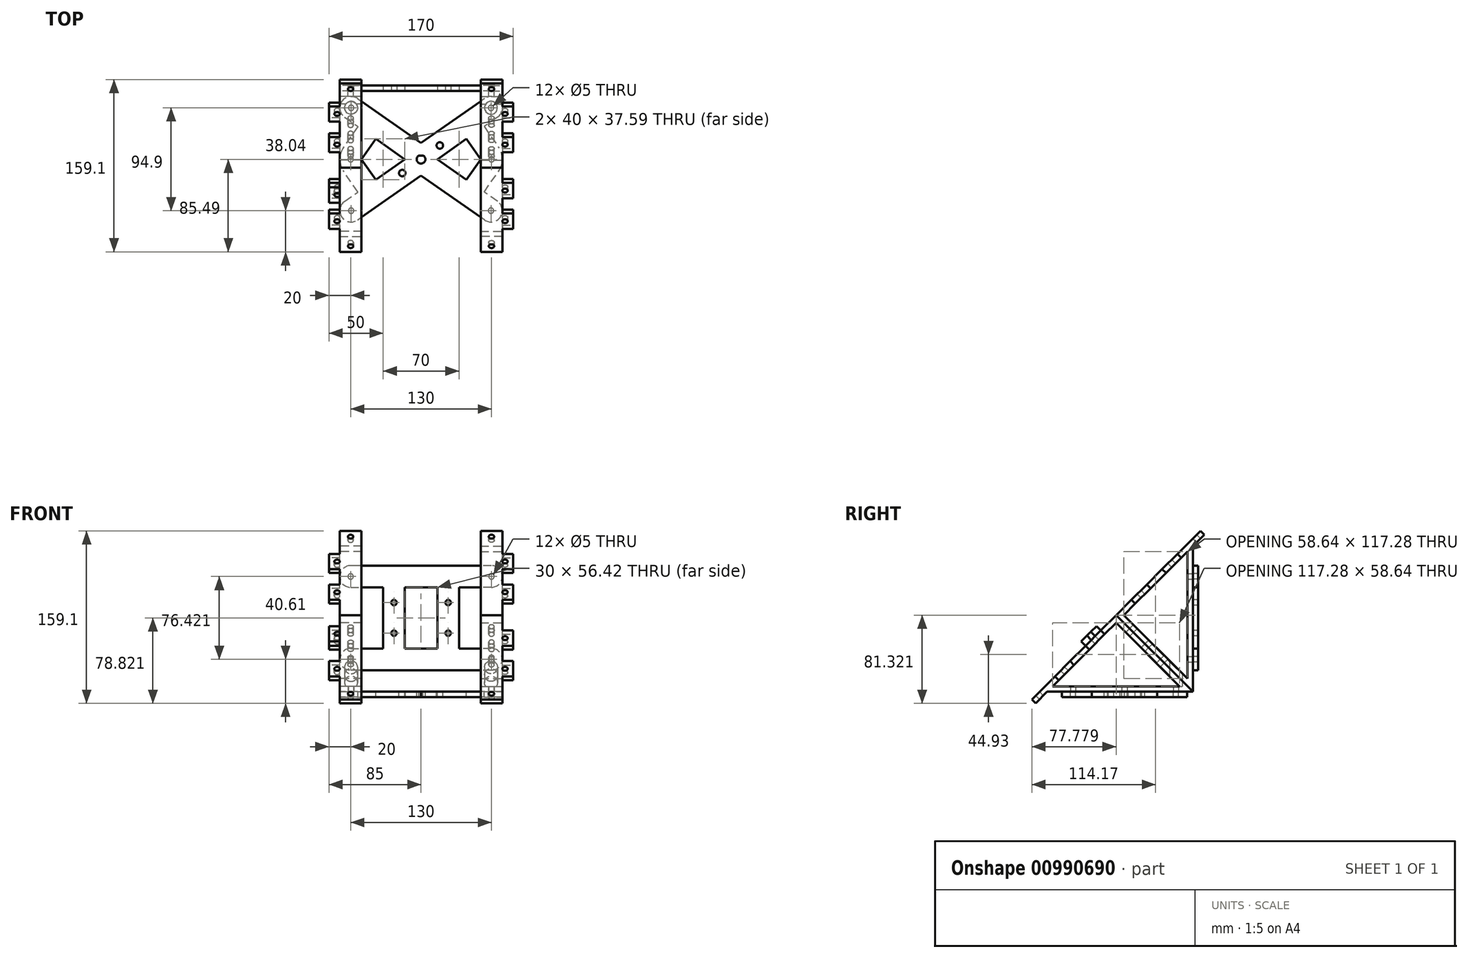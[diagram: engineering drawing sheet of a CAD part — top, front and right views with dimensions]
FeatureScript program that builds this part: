
annotation { "Feature Type Name" : "Feature", "Feature Type Description" : "" }
export const myFeature = defineFeature(function(context is Context, id is Id, definition is map)
    precondition{}
    {
        {
            var Q0;
            Q0=qCreatedBy(makeId("Right.planeOp"),FACE);
            var sketch = newSketch(context, id + "F0", { "sketchPlane" : qUnion([Q0])});
            skLineSegment(sketch, "E0", {"start": v(0, 0) * mm, "end": v(0, 141.42) * mm, "construction": true});
            skLineSegment(sketch, "E1", {"start": v(-141.42, 0) * mm, "end": v(0, 0) * mm});
            skLineSegment(sketch, "E2", {"start": v(0, 0) * mm, "end": v(-70.71, 70.71) * mm});
            skLineSegment(sketch, "E3", {"start": v(-141.42, 0) * mm, "end": v(-70.71, 70.71) * mm});
            skLineSegment(sketch, "E4", {"start": v(-70.71, 70.71) * mm, "end": v(0, 141.42) * mm, "construction": true});
            skLineSegment(sketch, "E5.0", {"start": v(-129.35, 5) * mm, "end": v(-70.71, 63.64) * mm});
            skLineSegment(sketch, "E5.1", {"start": v(-129.35, 5) * mm, "end": v(-12.07, 5) * mm});
            skLineSegment(sketch, "E5.2", {"start": v(-12.07, 5) * mm, "end": v(-70.71, 63.64) * mm});
            skLineSegment(sketch, "E6.0", {"start": v(-63.64, 70.71) * mm, "end": v(-5, 129.35) * mm, "construction": true});
            skLineSegment(sketch, "E6.1", {"start": v(-5, 12.07) * mm, "end": v(-63.64, 70.71) * mm, "construction": true});
            skLineSegment(sketch, "E6.2", {"start": v(-5, 12.07) * mm, "end": v(-5, 129.35) * mm, "construction": true});
            skSolve(sketch);
        }
        {
            var Q0;
            Q0=qCreatedBy(makeId("Right.planeOp"),FACE);
            var sketch = newSketch(context, id + "F1", { "sketchPlane" : qUnion([Q0])});
            skLineSegment(sketch, "E7", {"start": v(0, 0) * mm, "end": v(0, 141.42) * mm});
            skLineSegment(sketch, "E8", {"start": v(-141.42, 0) * mm, "end": v(0, 0) * mm, "construction": true});
            skLineSegment(sketch, "E9", {"start": v(0, 0) * mm, "end": v(-70.71, 70.71) * mm});
            skLineSegment(sketch, "E10", {"start": v(-141.42, 0) * mm, "end": v(-70.71, 70.71) * mm, "construction": true});
            skLineSegment(sketch, "E11", {"start": v(-70.71, 70.71) * mm, "end": v(0, 141.42) * mm});
            skLineSegment(sketch, "E12.0", {"start": v(-129.35, 5) * mm, "end": v(-70.71, 63.64) * mm, "construction": true});
            skLineSegment(sketch, "E12.1", {"start": v(-129.35, 5) * mm, "end": v(-12.07, 5) * mm, "construction": true});
            skLineSegment(sketch, "E12.2", {"start": v(-12.07, 5) * mm, "end": v(-70.71, 63.64) * mm, "construction": true});
            skLineSegment(sketch, "E13.0", {"start": v(-63.64, 70.71) * mm, "end": v(-5, 129.35) * mm});
            skLineSegment(sketch, "E13.1", {"start": v(-5, 12.07) * mm, "end": v(-63.64, 70.71) * mm});
            skLineSegment(sketch, "E13.2", {"start": v(-5, 12.07) * mm, "end": v(-5, 129.35) * mm});
            skSolve(sketch);
        }
        {
            var Q0;
            Q0 = qSketchRegion(id + "F0", true);
            extrude(context, id + "F2", {"entities" : qUnion([Q0]), "depth" : 20 * mm, "offsetDistance" : 25 * mm});
        }
        {
            var Q0;
            Q0 = qSketchRegion(id + "F1", true);
            extrude(context, id + "F3", {"entities" : qUnion([Q0]), "depth" : 20 * mm, "offsetDistance" : 25 * mm});
        }
        {
            var Q0;
            Q0=qCreatedBy(makeId("Top.planeOp"),FACE);
            var sketch = newSketch(context, id + "F4", { "sketchPlane" : qUnion([Q0])});
            skLineSegment(sketch, "E14", {"start": v(73.06, -59.5) * mm, "end": v(76.94, -59.5) * mm});
            skArc(sketch, "E15", {"start": v(73.06, -59.5) * mm, "mid": v(75, -67) * mm, "end": v(76.94, -59.5) * mm});
            skLineSegment(sketch, "E16.bottom", {"start": v(105, -93) * mm, "end": v(45, -93) * mm, "construction": true});
            skLineSegment(sketch, "E16.top", {"start": v(105, -33) * mm, "end": v(45, -33) * mm, "construction": true});
            skLineSegment(sketch, "E16.left", {"start": v(105, -93) * mm, "end": v(105, -33) * mm, "construction": true});
            skLineSegment(sketch, "E16.right", {"start": v(45, -93) * mm, "end": v(45, -33) * mm, "construction": true});
            skLineSegment(sketch, "E17", {"start": v(75, -63) * mm, "end": v(45, -63) * mm, "construction": true});
            skPoint(sketch, "E18.endSnap0", {"position": v(75, -93) * mm});
            skLineSegment(sketch, "E19", {"start": v(60, -63) * mm, "end": v(4.45, -101.9) * mm, "construction": true});
            skLineSegment(sketch, "E20", {"start": v(4.45, -101.9) * mm, "end": v(16.44, -119) * mm, "construction": true});
            skLineSegment(sketch, "E21", {"start": v(16.44, -119) * mm, "end": v(75, -78) * mm});
            skArc(sketch, "E22", {"start": v(4.45, -101.9) * mm, "mid": v(1.89, -116.44) * mm, "end": v(16.44, -119) * mm});
            skLineSegment(sketch, "E23", {"start": v(75, -63) * mm, "end": v(75, -93) * mm, "construction": true});
            skLineSegment(sketch, "E24.MirrorCS", {"start": v(75, -63) * mm, "end": v(105, -63) * mm, "construction": true});
            skLineSegment(sketch, "E25", {"start": v(60, -63) * mm, "end": v(33.16, -81.8) * mm});
            skLineSegment(sketch, "E26", {"start": v(33.16, -81.8) * mm, "end": v(20, -63) * mm});
            skLineSegment(sketch, "E27", {"start": v(4.45, -101.9) * mm, "end": v(16.78, -93.27) * mm});
            skLineSegment(sketch, "E28", {"start": v(16.78, -93.27) * mm, "end": v(3.62, -74.47) * mm});
            skArc(sketch, "E29", {"start": v(0, -63) * mm, "mid": v(0.93, -69.01) * mm, "end": v(3.62, -74.47) * mm});
            skArc(sketch, "E30.MirrorCS", {"start": v(150, -63) * mm, "mid": v(149.07, -69.01) * mm, "end": v(146.38, -74.47) * mm});
            skLineSegment(sketch, "E31.MirrorCS", {"start": v(145.55, -101.9) * mm, "end": v(133.56, -119) * mm, "construction": true});
            skLineSegment(sketch, "E32.MirrorCS", {"start": v(90, -63) * mm, "end": v(116.84, -81.8) * mm});
            skLineSegment(sketch, "E33.MirrorCS", {"start": v(145.55, -101.9) * mm, "end": v(133.22, -93.27) * mm});
            skArc(sketch, "E34.MirrorCS", {"start": v(145.55, -101.9) * mm, "mid": v(148.11, -116.44) * mm, "end": v(133.56, -119) * mm});
            skLineSegment(sketch, "E35.MirrorCS", {"start": v(133.22, -93.27) * mm, "end": v(146.38, -74.47) * mm});
            skLineSegment(sketch, "E36.MirrorCS", {"start": v(133.56, -119) * mm, "end": v(75, -78) * mm});
            skLineSegment(sketch, "E37.MirrorCS", {"start": v(116.84, -81.8) * mm, "end": v(130, -63) * mm});
            skLineSegment(sketch, "E38.MirrorCS", {"start": v(90, -63) * mm, "end": v(145.55, -101.9) * mm, "construction": true});
            skLineSegment(sketch, "E39.MirrorCS", {"start": v(45, -93) * mm, "end": v(105, -93) * mm, "construction": true});
            skPoint(sketch, "E40.MirrorP", {"position": v(75, -33) * mm});
            skLineSegment(sketch, "E41.MirrorCS", {"start": v(4.45, -24.1) * mm, "end": v(16.78, -32.73) * mm});
            skLineSegment(sketch, "E42.MirrorCS", {"start": v(90, -63) * mm, "end": v(116.84, -44.2) * mm});
            skLineSegment(sketch, "E43.MirrorCS", {"start": v(4.45, -24.1) * mm, "end": v(16.44, -7) * mm, "construction": true});
            skLineSegment(sketch, "E44.MirrorCS", {"start": v(145.55, -24.1) * mm, "end": v(133.56, -7) * mm, "construction": true});
            skLineSegment(sketch, "E45.MirrorCS", {"start": v(60, -63) * mm, "end": v(33.16, -44.2) * mm});
            skLineSegment(sketch, "E46.MirrorCS", {"start": v(145.55, -24.1) * mm, "end": v(133.22, -32.73) * mm});
            skLineSegment(sketch, "E47.MirrorCS", {"start": v(45, -33) * mm, "end": v(45, -93) * mm, "construction": true});
            skLineSegment(sketch, "E48.MirrorCS", {"start": v(105, -33) * mm, "end": v(105, -93) * mm, "construction": true});
            skLineSegment(sketch, "E49.MirrorCS", {"start": v(33.16, -44.2) * mm, "end": v(20, -63) * mm});
            skLineSegment(sketch, "E50.MirrorCS", {"start": v(16.78, -32.73) * mm, "end": v(3.62, -51.53) * mm});
            skArc(sketch, "E51.MirrorCS", {"start": v(145.55, -24.1) * mm, "mid": v(148.11, -9.56) * mm, "end": v(133.56, -7) * mm});
            skLineSegment(sketch, "E52.MirrorCS", {"start": v(60, -63) * mm, "end": v(4.45, -24.1) * mm, "construction": true});
            skArc(sketch, "E53.MirrorCS", {"start": v(4.45, -24.1) * mm, "mid": v(1.89, -9.56) * mm, "end": v(16.44, -7) * mm});
            skLineSegment(sketch, "E54.MirrorCS", {"start": v(116.84, -44.2) * mm, "end": v(130, -63) * mm});
            skLineSegment(sketch, "E55.MirrorCS", {"start": v(90, -63) * mm, "end": v(145.55, -24.1) * mm, "construction": true});
            skLineSegment(sketch, "E56.MirrorCS", {"start": v(133.22, -32.73) * mm, "end": v(146.38, -51.53) * mm});
            skLineSegment(sketch, "E57.MirrorCS", {"start": v(16.44, -7) * mm, "end": v(75, -48) * mm});
            skLineSegment(sketch, "E58.MirrorCS", {"start": v(45, -33) * mm, "end": v(105, -33) * mm, "construction": true});
            skLineSegment(sketch, "E59.MirrorCS", {"start": v(133.56, -7) * mm, "end": v(75, -48) * mm});
            skArc(sketch, "E60.MirrorCS", {"start": v(0, -63) * mm, "mid": v(0.93, -56.99) * mm, "end": v(3.62, -51.53) * mm});
            skArc(sketch, "E61.MirrorCS", {"start": v(150, -63) * mm, "mid": v(149.07, -56.99) * mm, "end": v(146.38, -51.53) * mm});
            skLineSegment(sketch, "E62.MirrorCS", {"start": v(75, -63) * mm, "end": v(75, -33) * mm, "construction": true});
            skCircle(sketch, "E63", {"center": v(10.45, -110.45) * mm, "radius": 2.5 * mm});
            skCircle(sketch, "E64.MirrorC", {"center": v(139.55, -110.45) * mm, "radius": 2.5 * mm});
            skCircle(sketch, "E65", {"center": v(10, -63) * mm, "radius": 2.5 * mm});
            skLineSegment(sketch, "E66", {"start": v(10.45, -110.45) * mm, "end": v(75, -63) * mm, "construction": true});
            skCircle(sketch, "E67.MirrorC", {"center": v(139.55, -15.55) * mm, "radius": 2.5 * mm});
            skCircle(sketch, "E68.MirrorC", {"center": v(10.45, -15.55) * mm, "radius": 2.5 * mm});
            skCircle(sketch, "E69", {"center": v(57.68, -75.73) * mm, "radius": 3 * mm});
            skCircle(sketch, "E70.1.0", {"center": v(92.32, -50.27) * mm, "radius": 3 * mm});
            skLineSegment(sketch, "E71", {"start": v(75, -63) * mm, "end": v(92.32, -50.27) * mm, "construction": true});
            skLineSegment(sketch, "E72", {"start": v(75, -63) * mm, "end": v(75, 0) * mm});
            skCircle(sketch, "E73.MirrorC", {"center": v(140, -63) * mm, "radius": 2.5 * mm});
            skSolve(sketch);
        }
        {
            var Q0;
            Q0=makeQuery(id+"F3.opExtrude","SWEPT_FACE",FACE,{"disambiguationData":[OSD([sQuery(id+"F1.wireOp",EDGE,"E7")])]});
            var sketch = newSketch(context, id + "F5", { "sketchPlane" : qUnion([Q0])});
            skLineSegment(sketch, "E74", {"start": v(-10, 141.42) * mm, "end": v(-10, 0) * mm, "construction": true});
            skCircle(sketch, "E75", {"center": v(-10, 106.42) * mm, "radius": 2.5 * mm});
            skCircle(sketch, "E76", {"center": v(-10, 30) * mm, "radius": 2.5 * mm});
            skSolve(sketch);
        }
        {
            var Q0;
            Q0 = qSketchRegion(id + "F5", true);
            extrude(context, id + "F6", {"entities" : qUnion([Q0]), "operationType" : NewBodyOperationType.REMOVE, "endBound" : BoundingType.UP_TO_NEXT, "oppositeDirection" : true, "depth" : 25 * mm, "offsetDistance" : 25 * mm});
        }
        {
            var Q0;
            Q0 = qSketchRegion(id + "F4", true);
            extrude(context, id + "F7", {"entities" : qUnion([Q0]), "oppositeDirection" : true, "depth" : 5 * mm, "offsetDistance" : 25 * mm});
        }
        {
            var Q0;
            Q0=makeQuery(id+"F3.opExtrude","SWEPT_FACE",FACE,{"disambiguationData":[OSD([sQuery(id+"F1.wireOp",EDGE,"E7")])]});
            var sketch = newSketch(context, id + "F8", { "sketchPlane" : qUnion([Q0])});
            skCircle(sketch, "E77", {"center": v(-10, 106.42) * mm, "radius": 2.5 * mm});
            skArc(sketch, "E78", {"start": v(-10, 116.42) * mm, "mid": v(0, 106.42) * mm, "end": v(-10, 96.42) * mm});
            skLineSegment(sketch, "E79", {"start": v(-10, 30) * mm, "end": v(-10, 106.42) * mm, "construction": true});
            skLineSegment(sketch, "E80", {"start": v(-10, 96.42) * mm, "end": v(-40, 96.42) * mm});
            skLineSegment(sketch, "E81", {"start": v(-40, 96.42) * mm, "end": v(-40, 68.21) * mm});
            skLineSegment(sketch, "E82", {"start": v(-10, 68.21) * mm, "end": v(-75, 68.21) * mm, "construction": true});
            skLineSegment(sketch, "E83", {"start": v(-75, 68.21) * mm, "end": v(-75, 116.42) * mm, "construction": true});
            skLineSegment(sketch, "E84", {"start": v(-75, 116.42) * mm, "end": v(-10, 116.42) * mm});
            skLineSegment(sketch, "E85", {"start": v(-60, 96.42) * mm, "end": v(-75, 96.42) * mm});
            skLineSegment(sketch, "E86", {"start": v(-60, 96.42) * mm, "end": v(-60, 68.21) * mm});
            skLineSegment(sketch, "E87.MirrorCS", {"start": v(-40, 40) * mm, "end": v(-40, 68.21) * mm});
            skLineSegment(sketch, "E88.MirrorCS", {"start": v(-60, 40) * mm, "end": v(-60, 68.21) * mm});
            skArc(sketch, "E89.MirrorCS", {"start": v(-10, 20) * mm, "mid": v(0, 30) * mm, "end": v(-10, 40) * mm});
            skLineSegment(sketch, "E90.MirrorCS", {"start": v(-75, 20) * mm, "end": v(-10, 20) * mm});
            skCircle(sketch, "E91.MirrorC", {"center": v(-10, 30) * mm, "radius": 2.5 * mm});
            skLineSegment(sketch, "E92.MirrorCS", {"start": v(-10, 40) * mm, "end": v(-40, 40) * mm});
            skLineSegment(sketch, "E93.MirrorCS", {"start": v(-60, 40) * mm, "end": v(-75, 40) * mm});
            skArc(sketch, "E94.MirrorCS", {"start": v(-140, 116.42) * mm, "mid": v(-150, 106.42) * mm, "end": v(-140, 96.42) * mm});
            skArc(sketch, "E95.MirrorCS", {"start": v(-140, 20) * mm, "mid": v(-150, 30) * mm, "end": v(-140, 40) * mm});
            skCircle(sketch, "E96.MirrorC", {"center": v(-140, 106.42) * mm, "radius": 2.5 * mm});
            skLineSegment(sketch, "E97.MirrorCS", {"start": v(-90, 96.42) * mm, "end": v(-75, 96.42) * mm});
            skLineSegment(sketch, "E98.MirrorCS", {"start": v(-75, 116.42) * mm, "end": v(-140, 116.42) * mm});
            skLineSegment(sketch, "E99.MirrorCS", {"start": v(-90, 40) * mm, "end": v(-90, 68.21) * mm});
            skLineSegment(sketch, "E100.MirrorCS", {"start": v(-90, 40) * mm, "end": v(-75, 40) * mm});
            skLineSegment(sketch, "E101.MirrorCS", {"start": v(-90, 96.42) * mm, "end": v(-90, 68.21) * mm});
            skLineSegment(sketch, "E102.MirrorCS", {"start": v(-75, 20) * mm, "end": v(-140, 20) * mm});
            skLineSegment(sketch, "E103.MirrorCS", {"start": v(-140, 68.21) * mm, "end": v(-75, 68.21) * mm, "construction": true});
            skCircle(sketch, "E104.MirrorC", {"center": v(-140, 30) * mm, "radius": 2.5 * mm});
            skLineSegment(sketch, "E105.MirrorCS", {"start": v(-140, 40) * mm, "end": v(-110, 40) * mm});
            skLineSegment(sketch, "E106.MirrorCS", {"start": v(-140, 30) * mm, "end": v(-140, 106.42) * mm, "construction": true});
            skLineSegment(sketch, "E107.MirrorCS", {"start": v(-110, 96.42) * mm, "end": v(-110, 68.21) * mm});
            skLineSegment(sketch, "E108.MirrorCS", {"start": v(-110, 40) * mm, "end": v(-110, 68.21) * mm});
            skLineSegment(sketch, "E109.MirrorCS", {"start": v(-140, 96.42) * mm, "end": v(-110, 96.42) * mm});
            skCircle(sketch, "E110", {"center": v(-100, 82.32) * mm, "radius": 2.5 * mm});
            skLineSegment(sketch, "E111", {"start": v(-110, 82.32) * mm, "end": v(-90, 82.32) * mm, "construction": true});
            skCircle(sketch, "E112.MirrorC", {"center": v(-50, 82.32) * mm, "radius": 2.5 * mm});
            skCircle(sketch, "E113.MirrorC", {"center": v(-100, 54.1) * mm, "radius": 2.5 * mm});
            skCircle(sketch, "E114.MirrorC", {"center": v(-50, 54.1) * mm, "radius": 2.5 * mm});
            skSolve(sketch);
        }
        {
            var Q0;
            Q0 = qSketchRegion(id + "F8", true);
            extrude(context, id + "F9", {"entities" : qUnion([Q0]), "depth" : 5 * mm, "offsetDistance" : 25 * mm});
        }
        {
            var Q0;
            Q0=makeQuery(id+"F2.opExtrude","SWEPT_FACE",FACE,{"disambiguationData":[OSD([sQuery(id+"F0.wireOp",EDGE,"E1")])]});
            var sketch = newSketch(context, id + "F10", { "sketchPlane" : qUnion([Q0])});
            skCircle(sketch, "E115", {"center": v(10.45, 110.45) * mm, "radius": 2.5 * mm});
            skCircle(sketch, "E116", {"center": v(10, 63) * mm, "radius": 2.5 * mm});
            skCircle(sketch, "E117", {"center": v(10.45, 15.55) * mm, "radius": 2.5 * mm});
            skSolve(sketch);
        }
        {
            var Q0;
            Q0 = qSketchRegion(id + "F10", true);
            extrude(context, id + "F11", {"entities" : qUnion([Q0]), "operationType" : NewBodyOperationType.REMOVE, "endBound" : BoundingType.UP_TO_NEXT, "oppositeDirection" : true, "depth" : 25 * mm, "offsetDistance" : 25 * mm});
        }
        {
            var Q0;
            Q0=qCreatedBy(makeId("Right.planeOp"),FACE);
            cPlane(context, id + "F12", {"entities" : qUnion([Q0]), "cplaneType" : CPlaneType.OFFSET, "offset" : 75 * mm, "width" : 150 * mm, "height" : 150 * mm});
        }
        {
            var Q0;
            Q0=makeQuery(id+"F3.opExtrude","SWEPT_FACE",FACE,{"disambiguationData":[OSD([sQuery(id+"F1.wireOp",EDGE,"E11")])]});
            var sketch = newSketch(context, id + "F13", { "sketchPlane" : qUnion([Q0])});
            skLineSegment(sketch, "E118.bottom", {"start": v(0, 80) * mm, "end": v(-10, 80) * mm});
            skLineSegment(sketch, "E118.top", {"start": v(0, 60) * mm, "end": v(-10, 60) * mm});
            skLineSegment(sketch, "E118.left", {"start": v(0, 80) * mm, "end": v(0, 60) * mm});
            skLineSegment(sketch, "E118.right", {"start": v(-10, 80) * mm, "end": v(-10, 60) * mm});
            skLineSegment(sketch, "E119", {"start": v(0, 50) * mm, "end": v(20, 50) * mm, "construction": true});
            skLineSegment(sketch, "E120.MirrorCS", {"start": v(-10, 20) * mm, "end": v(-10, 40) * mm});
            skLineSegment(sketch, "E121.MirrorCS", {"start": v(0, 20) * mm, "end": v(0, 40) * mm});
            skLineSegment(sketch, "E122.MirrorCS", {"start": v(0, 20) * mm, "end": v(-10, 20) * mm});
            skLineSegment(sketch, "E123.MirrorCS", {"start": v(0, 40) * mm, "end": v(-10, 40) * mm});
            skLineSegment(sketch, "E124.bottom", {"start": v(0, 87.93) * mm, "end": v(20, 87.93) * mm});
            skLineSegment(sketch, "E124.top", {"start": v(0, 110) * mm, "end": v(20, 110) * mm});
            skLineSegment(sketch, "E124.left", {"start": v(0, 87.93) * mm, "end": v(0, 110) * mm});
            skLineSegment(sketch, "E124.right", {"start": v(20, 87.93) * mm, "end": v(20, 110) * mm});
            skCircle(sketch, "E125", {"center": v(10, 102.5) * mm, "radius": 2.5 * mm});
            skPoint(sketch, "E125.centerSnap0", {"position": v(10, 100) * mm});
            skSolve(sketch);
        }
        {
            var Q0;
            Q0 = qSketchRegion(id + "F13", true);
            extrude(context, id + "F14", {"entities" : qUnion([Q0]), "operationType" : NewBodyOperationType.ADD, "oppositeDirection" : true, "depth" : 5 * mm, "offsetDistance" : 25 * mm});
        }
        {
            var Q0;
            Q0=makeQuery(id+"F14.boolean.opBoolean","MERGE",FACE,{"derivedFrom":[makeQuery(id+"F3.opExtrude","SWEPT_FACE",FACE,{"disambiguationData":[OSD([sQuery(id+"F1.wireOp",EDGE,"E11")])]}),makeQuery(id+"F14.opExtrude","CAP_FACE",FACE,{"disambiguationData":[OSD([sQuery(id+"F13.wireOp",EDGE,"E118.bottom"),sQuery(id+"F13.wireOp",EDGE,"E118.top"),sQuery(id+"F13.wireOp",EDGE,"E118.left"),sQuery(id+"F13.wireOp",EDGE,"E118.right")])],"isStart":true}),makeQuery(id+"F14.opExtrude","CAP_FACE",FACE,{"disambiguationData":[OSD([sQuery(id+"F13.wireOp",EDGE,"E120.MirrorCS"),sQuery(id+"F13.wireOp",EDGE,"E121.MirrorCS"),sQuery(id+"F13.wireOp",EDGE,"E122.MirrorCS"),sQuery(id+"F13.wireOp",EDGE,"E123.MirrorCS")])],"isStart":true})]});
            var sketch = newSketch(context, id + "F15", { "sketchPlane" : qUnion([Q0])});
            skLineSegment(sketch, "E126", {"start": v(0, 80) * mm, "end": v(0, 60) * mm, "construction": true});
            skCircle(sketch, "E127", {"center": v(-2.5, 70) * mm, "radius": 2.5 * mm});
            skPoint(sketch, "E127.centerSnap0", {"position": v(0, 70) * mm});
            skLineSegment(sketch, "E128", {"start": v(0, 50) * mm, "end": v(20.74, 50) * mm, "construction": true});
            skCircle(sketch, "E129.MirrorC", {"center": v(-2.5, 30) * mm, "radius": 2.5 * mm});
            skSolve(sketch);
        }
        {
            var Q0;
            Q0 = qSketchRegion(id + "F15", true);
            extrude(context, id + "F16", {"entities" : qUnion([Q0]), "operationType" : NewBodyOperationType.REMOVE, "endBound" : BoundingType.UP_TO_NEXT, "oppositeDirection" : true, "depth" : 25 * mm, "offsetDistance" : 25 * mm});
        }
        {
            var Q0;
            Q0=makeQuery(id+"F2.opExtrude","SWEPT_FACE",FACE,{"disambiguationData":[OSD([sQuery(id+"F0.wireOp",EDGE,"E3")])]});
            var sketch = newSketch(context, id + "F17", { "sketchPlane" : qUnion([Q0])});
            skLineSegment(sketch, "E130.bottom", {"start": v(0, -80) * mm, "end": v(-10, -80) * mm});
            skLineSegment(sketch, "E130.top", {"start": v(0, -60) * mm, "end": v(-10, -60) * mm});
            skLineSegment(sketch, "E130.left", {"start": v(0, -80) * mm, "end": v(0, -60) * mm});
            skLineSegment(sketch, "E130.right", {"start": v(-10, -80) * mm, "end": v(-10, -60) * mm});
            skPoint(sketch, "E131.centerSnap0", {"position": v(0, -70) * mm});
            skLineSegment(sketch, "E132", {"start": v(0, -50) * mm, "end": v(20, -50) * mm, "construction": true});
            skLineSegment(sketch, "E133.MirrorCS", {"start": v(0, -20) * mm, "end": v(-10, -20) * mm});
            skLineSegment(sketch, "E134.MirrorCS", {"start": v(0, -20) * mm, "end": v(0, -40) * mm});
            skLineSegment(sketch, "E135.MirrorCS", {"start": v(-10, -20) * mm, "end": v(-10, -40) * mm});
            skLineSegment(sketch, "E136.MirrorCS", {"start": v(0, -40) * mm, "end": v(-10, -40) * mm});
            skLineSegment(sketch, "E137.bottom", {"start": v(0, -87.93) * mm, "end": v(20, -87.93) * mm});
            skLineSegment(sketch, "E137.top", {"start": v(0, -110) * mm, "end": v(20, -110) * mm});
            skLineSegment(sketch, "E137.left", {"start": v(0, -87.93) * mm, "end": v(0, -110) * mm});
            skLineSegment(sketch, "E137.right", {"start": v(20, -87.93) * mm, "end": v(20, -110) * mm});
            skCircle(sketch, "E138", {"center": v(10, -102.5) * mm, "radius": 2.5 * mm});
            skPoint(sketch, "E138.centerSnap0", {"position": v(10, -100) * mm});
            skSolve(sketch);
        }
        {
            var Q0;
            Q0 = qSketchRegion(id + "F17", true);
            extrude(context, id + "F18", {"entities" : qUnion([Q0]), "operationType" : NewBodyOperationType.ADD, "oppositeDirection" : true, "depth" : 5 * mm, "offsetDistance" : 25 * mm});
        }
        {
            var Q0;
            Q0=makeQuery(id+"F18.boolean.opBoolean","MERGE",FACE,{"derivedFrom":[makeQuery(id+"F2.opExtrude","SWEPT_FACE",FACE,{"disambiguationData":[OSD([sQuery(id+"F0.wireOp",EDGE,"E3")])]}),makeQuery(id+"F18.opExtrude","CAP_FACE",FACE,{"disambiguationData":[OSD([sQuery(id+"F17.wireOp",EDGE,"E130.bottom"),sQuery(id+"F17.wireOp",EDGE,"E130.top"),sQuery(id+"F17.wireOp",EDGE,"E130.left"),sQuery(id+"F17.wireOp",EDGE,"E130.right")])],"isStart":true}),makeQuery(id+"F18.opExtrude","CAP_FACE",FACE,{"disambiguationData":[OSD([sQuery(id+"F17.wireOp",EDGE,"E133.MirrorCS"),sQuery(id+"F17.wireOp",EDGE,"E134.MirrorCS"),sQuery(id+"F17.wireOp",EDGE,"E135.MirrorCS"),sQuery(id+"F17.wireOp",EDGE,"E136.MirrorCS")])],"isStart":true}),makeQuery(id+"F18.opExtrude","CAP_FACE",FACE,{"disambiguationData":[OSD([sQuery(id+"F17.wireOp",EDGE,"E137.bottom"),sQuery(id+"F17.wireOp",EDGE,"E137.top"),sQuery(id+"F17.wireOp",EDGE,"E137.left"),sQuery(id+"F17.wireOp",EDGE,"E137.right"),sQuery(id+"F17.wireOp",EDGE,"E138")])],"isStart":true})]});
            var sketch = newSketch(context, id + "F19", { "sketchPlane" : qUnion([Q0])});
            skLineSegment(sketch, "E139", {"start": v(0, -20) * mm, "end": v(0, -40) * mm, "construction": true});
            skLineSegment(sketch, "E140", {"start": v(0, -50) * mm, "end": v(20, -50) * mm, "construction": true});
            skCircle(sketch, "E141", {"center": v(-2.5, -30) * mm, "radius": 2.5 * mm});
            skPoint(sketch, "E141.centerSnap0", {"position": v(0, -30) * mm});
            skCircle(sketch, "E142.MirrorC", {"center": v(-2.5, -70) * mm, "radius": 2.5 * mm});
            skSolve(sketch);
        }
        {
            var Q0;
            Q0 = qSketchRegion(id + "F19", true);
            extrude(context, id + "F20", {"entities" : qUnion([Q0]), "operationType" : NewBodyOperationType.REMOVE, "endBound" : BoundingType.UP_TO_NEXT, "oppositeDirection" : true, "depth" : 25 * mm, "offsetDistance" : 25 * mm});
        }
        {
            var Q0;
            Q0=makeQuery(id+"F3.opExtrude","SWEPT_FACE",FACE,{"disambiguationData":[OSD([sQuery(id+"F1.wireOp",EDGE,"E13.1")])]});
            var sketch = newSketch(context, id + "F21", { "sketchPlane" : qUnion([Q0])});
            skCircle(sketch, "E143", {"center": v(-10, 80) * mm, "radius": 2.5 * mm});
            skPoint(sketch, "E143.centerSnap0", {"position": v(-10, 95) * mm});
            skCircle(sketch, "E144.0.1.0", {"center": v(-10, 60) * mm, "radius": 2.5 * mm});
            skCircle(sketch, "E144.0.2.0", {"center": v(-10, 40) * mm, "radius": 2.5 * mm});
            skLineSegment(sketch, "E144.direction1", {"start": v(-10, 80) * mm, "end": v(15, 80) * mm, "construction": true});
            skLineSegment(sketch, "E144.direction2", {"start": v(-10, 80) * mm, "end": v(-10, 60) * mm, "construction": true});
            skSolve(sketch);
        }
        {
            var Q0;
            Q0 = qSketchRegion(id + "F21", true);
            extrude(context, id + "F22", {"entities" : qUnion([Q0]), "operationType" : NewBodyOperationType.REMOVE, "oppositeDirection" : true, "depth" : 10 * mm, "offsetDistance" : 25 * mm});
        }
        {
            var Q0;
            Q0=makeQuery(id+"F2.opExtrude","SWEPT_FACE",FACE,{"disambiguationData":[OSD([sQuery(id+"F0.wireOp",EDGE,"E5.1")])]});
            var sketch = newSketch(context, id + "F23", { "sketchPlane" : qUnion([Q0])});
            skCircle(sketch, "E145", {"center": v(10.45, -15.55) * mm, "radius": 6 * mm});
            skSolve(sketch);
        }
        {
            var Q0;
            Q0 = qSketchRegion(id + "F23", true);
            extrude(context, id + "F24", {"entities" : qUnion([Q0]), "operationType" : NewBodyOperationType.REMOVE, "depth" : 25 * mm, "offsetDistance" : 25 * mm});
        }
        {
            var Q0;
            Q0=makeQuery(id+"F2.opExtrude","SWEPT_BODY",BODY,{"disambiguationData":[OSD([sQuery(id+"F0.wireOp",EDGE,"E1"),sQuery(id+"F0.wireOp",EDGE,"E2"),sQuery(id+"F0.wireOp",EDGE,"E3"),sQuery(id+"F0.wireOp",EDGE,"E5.0"),sQuery(id+"F0.wireOp",EDGE,"E5.1"),sQuery(id+"F0.wireOp",EDGE,"E5.2")])]});
            var Q1;
            Q1=makeQuery(id+"F3.opExtrude","SWEPT_BODY",BODY,{"disambiguationData":[OSD([sQuery(id+"F1.wireOp",EDGE,"E7"),sQuery(id+"F1.wireOp",EDGE,"E9"),sQuery(id+"F1.wireOp",EDGE,"E11"),sQuery(id+"F1.wireOp",EDGE,"E13.0"),sQuery(id+"F1.wireOp",EDGE,"E13.1"),sQuery(id+"F1.wireOp",EDGE,"E13.2")])]});
            var Q2;
            Q2=qCreatedBy(id+"F12.planeOp",FACE);
            mirror(context, id + "F25", {"entities" : qUnion([Q0, Q1]), "mirrorPlane" : qUnion([Q2])});
        }
        {
            var Q0;
            Q0=makeQuery(id+"F18.boolean.opBoolean","MERGE",FACE,{"derivedFrom":[makeQuery(id+"F2.opExtrude","SWEPT_FACE",FACE,{"disambiguationData":[OSD([sQuery(id+"F0.wireOp",EDGE,"E3")])]}),makeQuery(id+"F18.opExtrude","CAP_FACE",FACE,{"disambiguationData":[OSD([sQuery(id+"F17.wireOp",EDGE,"E130.bottom"),sQuery(id+"F17.wireOp",EDGE,"E130.top"),sQuery(id+"F17.wireOp",EDGE,"E130.left"),sQuery(id+"F17.wireOp",EDGE,"E130.right")])],"isStart":true}),makeQuery(id+"F18.opExtrude","CAP_FACE",FACE,{"disambiguationData":[OSD([sQuery(id+"F17.wireOp",EDGE,"E133.MirrorCS"),sQuery(id+"F17.wireOp",EDGE,"E134.MirrorCS"),sQuery(id+"F17.wireOp",EDGE,"E135.MirrorCS"),sQuery(id+"F17.wireOp",EDGE,"E136.MirrorCS")])],"isStart":true}),makeQuery(id+"F18.opExtrude","CAP_FACE",FACE,{"disambiguationData":[OSD([sQuery(id+"F17.wireOp",EDGE,"E137.bottom"),sQuery(id+"F17.wireOp",EDGE,"E137.top"),sQuery(id+"F17.wireOp",EDGE,"E137.left"),sQuery(id+"F17.wireOp",EDGE,"E137.right"),sQuery(id+"F17.wireOp",EDGE,"E138")])],"isStart":true})]});
            var sketch = newSketch(context, id + "F26", { "sketchPlane" : qUnion([Q0])});
            skLineSegment(sketch, "E146", {"start": v(0, -20) * mm, "end": v(-10, -20) * mm});
            skLineSegment(sketch, "E147", {"start": v(-10, -20) * mm, "end": v(-10, -40) * mm});
            skLineSegment(sketch, "E148", {"start": v(-10, -40) * mm, "end": v(0, -40) * mm});
            skLineSegment(sketch, "E149", {"start": v(0, -40) * mm, "end": v(0, -32.5) * mm});
            skLineSegment(sketch, "E150", {"start": v(0, -20) * mm, "end": v(0, -27.5) * mm});
            skLineSegment(sketch, "E151", {"start": v(0, -27.5) * mm, "end": v(-2.5, -27.5) * mm});
            skArc(sketch, "E152", {"start": v(-2.5, -27.5) * mm, "mid": v(-5, -30) * mm, "end": v(-2.5, -32.5) * mm});
            skLineSegment(sketch, "E153", {"start": v(0, -32.5) * mm, "end": v(-2.5, -32.5) * mm});
            skSolve(sketch);
        }
        {
            var Q0;
            Q0=makeQuery(id+"F26.imprint","IMPRINT",FACE,{"disambiguationData":[TD([[makeQuery(id+"F26.imprint","IMPRINT",EDGE,{"derivedFrom":sQuery(id+"F26.wireOp",EDGE,"E146")}),1.0]])]});
            extrude(context, id + "F27", {"entities" : qUnion([Q0]), "depth" : 5.7 * mm, "offsetDistance" : 25 * mm});
        }
    });
